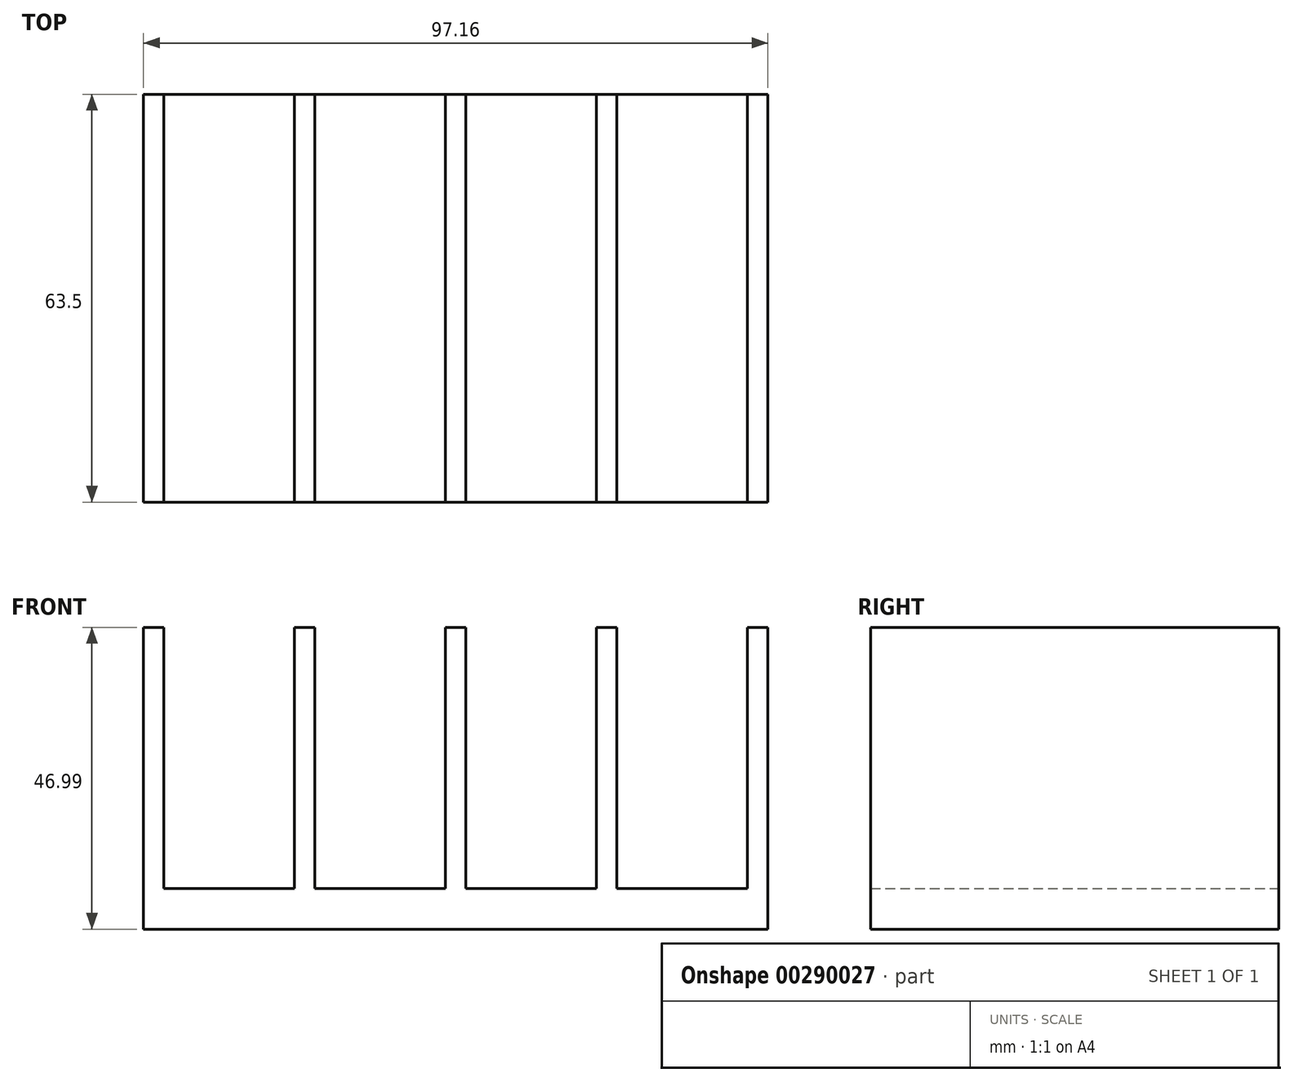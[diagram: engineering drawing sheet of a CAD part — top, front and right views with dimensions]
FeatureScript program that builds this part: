
annotation { "Feature Type Name" : "Feature", "Feature Type Description" : "" }
export const myFeature = defineFeature(function(context is Context, id is Id, definition is map)
    precondition{}
    {
        {
            var Q0;
            Q0=qCreatedBy(makeId("Front.planeOp"),FACE);
            var sketch = newSketch(context, id + "F0", { "sketchPlane" : qUnion([Q0])});
            skLineSegment(sketch, "E0.bottom", {"start": v(48.58, 3.18) * mm, "end": v(-48.58, 3.18) * mm});
            skLineSegment(sketch, "E0.top", {"start": v(48.58, -3.18) * mm, "end": v(-48.58, -3.18) * mm});
            skLineSegment(sketch, "E0.left", {"start": v(48.58, 3.18) * mm, "end": v(48.58, -3.18) * mm});
            skLineSegment(sketch, "E0.right", {"start": v(-48.58, 3.18) * mm, "end": v(-48.58, -3.18) * mm});
            skPoint(sketch, "E0.middle", {"position": v(0, 0) * mm});
            skLineSegment(sketch, "E1.bottom", {"start": v(-48.58, 3.18) * mm, "end": v(-45.4, 3.18) * mm});
            skLineSegment(sketch, "E1.top", {"start": v(-48.58, 43.82) * mm, "end": v(-45.4, 43.82) * mm});
            skLineSegment(sketch, "E1.left", {"start": v(-48.58, 3.18) * mm, "end": v(-48.58, 43.82) * mm});
            skLineSegment(sketch, "E1.right", {"start": v(-45.4, 3.18) * mm, "end": v(-45.4, 43.82) * mm});
            skLineSegment(sketch, "E2.bottom", {"start": v(-25.08, 3.18) * mm, "end": v(-21.9, 3.18) * mm});
            skLineSegment(sketch, "E2.top", {"start": v(-25.08, 43.82) * mm, "end": v(-21.9, 43.82) * mm});
            skLineSegment(sketch, "E2.left", {"start": v(-25.08, 3.17) * mm, "end": v(-25.08, 43.81) * mm});
            skLineSegment(sketch, "E2.right", {"start": v(-21.9, 3.17) * mm, "end": v(-21.9, 43.81) * mm});
            skLineSegment(sketch, "E3.bottom", {"start": v(-1.59, 3.18) * mm, "end": v(1.59, 3.18) * mm});
            skLineSegment(sketch, "E3.top", {"start": v(-1.59, 43.82) * mm, "end": v(1.59, 43.82) * mm});
            skLineSegment(sketch, "E3.left", {"start": v(-1.59, 3.17) * mm, "end": v(-1.59, 43.81) * mm});
            skLineSegment(sketch, "E3.right", {"start": v(1.59, 3.17) * mm, "end": v(1.59, 43.81) * mm});
            skLineSegment(sketch, "E4.bottom", {"start": v(21.9, 3.18) * mm, "end": v(25.08, 3.18) * mm});
            skLineSegment(sketch, "E4.top", {"start": v(21.9, 43.82) * mm, "end": v(25.08, 43.82) * mm});
            skLineSegment(sketch, "E4.left", {"start": v(21.9, 3.17) * mm, "end": v(21.9, 43.81) * mm});
            skLineSegment(sketch, "E4.right", {"start": v(25.08, 3.17) * mm, "end": v(25.08, 43.81) * mm});
            skLineSegment(sketch, "E5.bottom", {"start": v(48.58, 3.18) * mm, "end": v(48.58, 3.18) * mm});
            skLineSegment(sketch, "E6.bottom", {"start": v(48.58, 3.18) * mm, "end": v(45.4, 3.18) * mm});
            skLineSegment(sketch, "E6.top", {"start": v(48.58, 43.82) * mm, "end": v(45.4, 43.82) * mm});
            skLineSegment(sketch, "E6.left", {"start": v(48.58, 3.18) * mm, "end": v(48.58, 43.82) * mm});
            skLineSegment(sketch, "E6.right", {"start": v(45.4, 3.18) * mm, "end": v(45.4, 43.82) * mm});
            skSolve(sketch);
        }
        {
            var Q0;
            Q0 = qSketchRegion(id + "F0", true);
            extrude(context, id + "F1", {"entities" : qUnion([Q0]), "depth" : 63.5 * mm});
        }
    });
